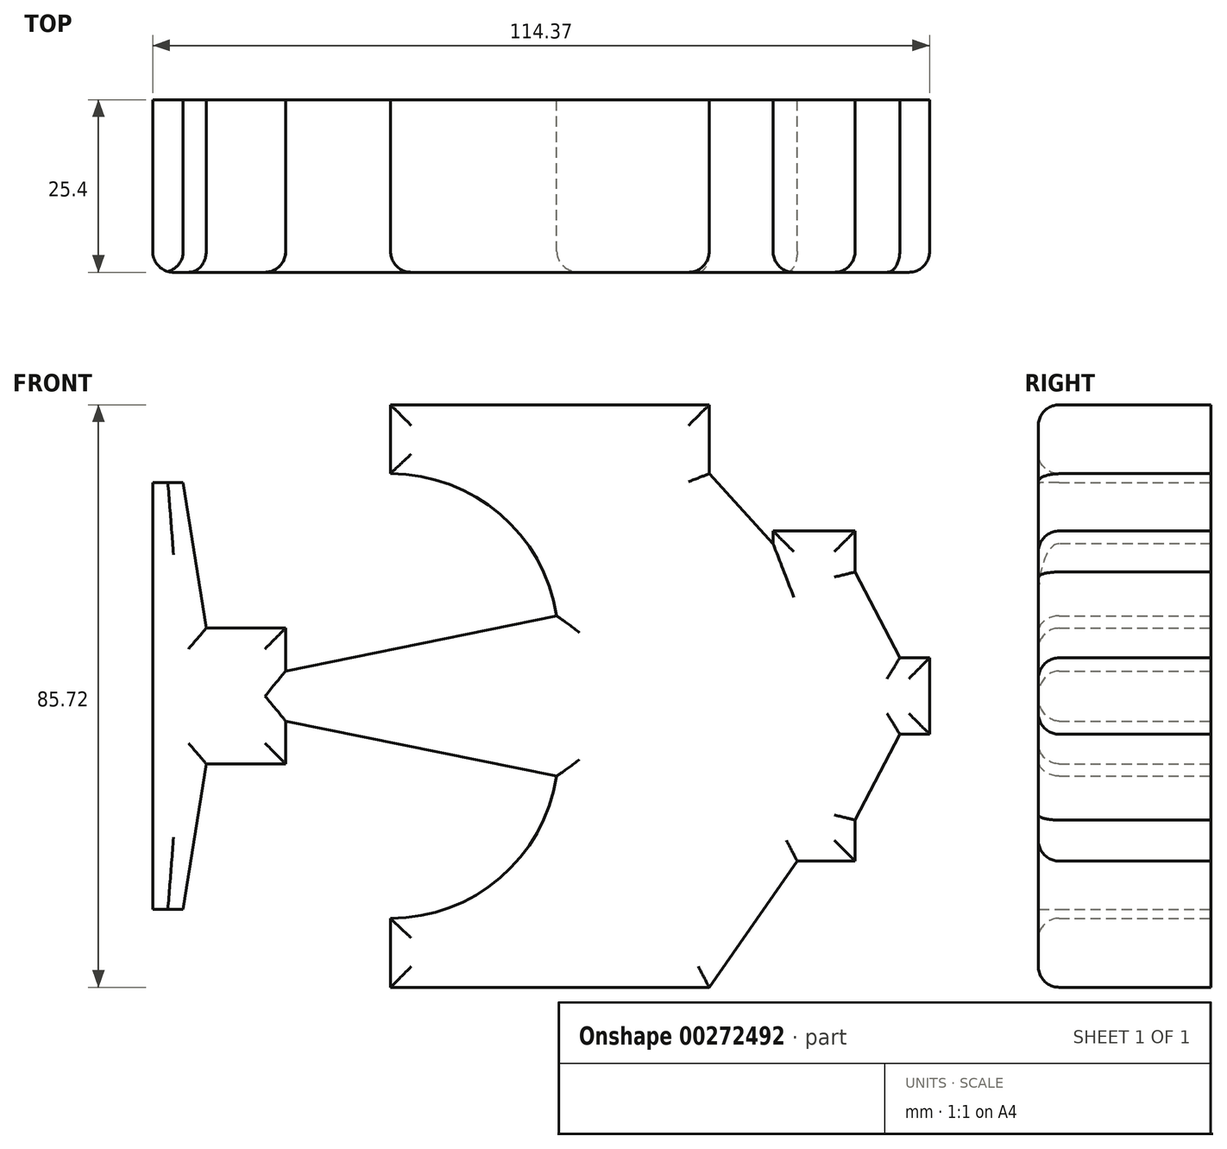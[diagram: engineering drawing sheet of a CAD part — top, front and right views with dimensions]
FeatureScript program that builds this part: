
annotation { "Feature Type Name" : "Feature", "Feature Type Description" : "" }
export const myFeature = defineFeature(function(context is Context, id is Id, definition is map)
    precondition{}
    {
        {
            var Q0;
            Q0=qCreatedBy(makeId("Front.planeOp"),FACE);
            var sketch = newSketch(context, id + "F0", { "sketchPlane" : qUnion([Q0])});
            skLineSegment(sketch, "E0.bottom", {"start": v(38.9, 3.7) * mm, "end": v(-38.9, 3.7) * mm});
            skLineSegment(sketch, "E0.top", {"start": v(38.9, -3.7) * mm, "end": v(-38.9, -3.7) * mm});
            skLineSegment(sketch, "E0.left", {"start": v(38.9, 3.7) * mm, "end": v(38.9, -3.7) * mm});
            skLineSegment(sketch, "E0.right", {"start": v(-38.9, 3.7) * mm, "end": v(-38.9, -3.7) * mm});
            skPoint(sketch, "E0.middle", {"position": v(0, 0) * mm});
            skLineSegment(sketch, "E1.bottom", {"start": v(32.86, -24.29) * mm, "end": v(44.93, -24.29) * mm});
            skLineSegment(sketch, "E1.top", {"start": v(32.86, -18.25) * mm, "end": v(44.93, -18.25) * mm});
            skLineSegment(sketch, "E1.left", {"start": v(32.86, -24.29) * mm, "end": v(32.86, -18.25) * mm});
            skLineSegment(sketch, "E1.right", {"start": v(44.93, -24.29) * mm, "end": v(44.93, -18.25) * mm});
            skPoint(sketch, "E1.middle", {"position": v(38.9, -21.27) * mm});
            skLineSegment(sketch, "E2.MirrorCS", {"start": v(32.86, 18.25) * mm, "end": v(44.93, 18.25) * mm});
            skPoint(sketch, "E3.MirrorP", {"position": v(38.9, 21.27) * mm});
            skLineSegment(sketch, "E4.MirrorCS", {"start": v(44.93, 24.29) * mm, "end": v(44.93, 18.25) * mm});
            skLineSegment(sketch, "E5.MirrorCS", {"start": v(32.86, 24.29) * mm, "end": v(32.86, 18.25) * mm});
            skLineSegment(sketch, "E6.MirrorCS", {"start": v(32.86, 24.29) * mm, "end": v(44.93, 24.29) * mm});
            skLineSegment(sketch, "E7", {"start": v(44.93, -18.25) * mm, "end": v(38.9, -3.7) * mm});
            skLineSegment(sketch, "E8", {"start": v(44.93, 18.25) * mm, "end": v(38.9, 3.7) * mm});
            skLineSegment(sketch, "E9", {"start": v(32.86, -18.25) * mm, "end": v(-38.9, -3.7) * mm});
            skLineSegment(sketch, "E10", {"start": v(32.86, 18.25) * mm, "end": v(-38.9, 3.7) * mm});
            skLineSegment(sketch, "E11.bottom", {"start": v(51.51, 5.61) * mm, "end": v(55.9, 5.61) * mm});
            skLineSegment(sketch, "E11.top", {"start": v(51.51, -5.61) * mm, "end": v(55.9, -5.61) * mm});
            skLineSegment(sketch, "E11.left", {"start": v(51.51, 5.61) * mm, "end": v(51.51, -5.61) * mm});
            skLineSegment(sketch, "E11.right", {"start": v(55.9, 5.61) * mm, "end": v(55.9, -5.61) * mm});
            skPoint(sketch, "E11.middle", {"position": v(53.7, 0) * mm});
            skLineSegment(sketch, "E12", {"start": v(51.51, 5.61) * mm, "end": v(44.93, 18.25) * mm});
            skLineSegment(sketch, "E13", {"start": v(51.51, -5.61) * mm, "end": v(44.93, -18.25) * mm});
            skLineSegment(sketch, "E14.bottom", {"start": v(-38.9, 9.99) * mm, "end": v(-38.9, 9.99) * mm});
            skLineSegment(sketch, "E14.top", {"start": v(-38.9, -9.99) * mm, "end": v(-38.9, -9.99) * mm});
            skLineSegment(sketch, "E14.left", {"start": v(-38.9, 9.99) * mm, "end": v(-38.9, -9.99) * mm});
            skLineSegment(sketch, "E14.right", {"start": v(-38.9, 9.99) * mm, "end": v(-38.9, -9.99) * mm});
            skPoint(sketch, "E14.middle", {"position": v(-38.9, 0) * mm});
            skLineSegment(sketch, "E15.bottom", {"start": v(-47.82, 9.99) * mm, "end": v(-50.58, 9.99) * mm});
            skLineSegment(sketch, "E15.top", {"start": v(-47.82, -9.99) * mm, "end": v(-50.58, -9.99) * mm});
            skLineSegment(sketch, "E15.left", {"start": v(-47.82, 9.99) * mm, "end": v(-47.82, -9.99) * mm});
            skLineSegment(sketch, "E15.right", {"start": v(-50.58, 9.99) * mm, "end": v(-50.58, -9.99) * mm});
            skPoint(sketch, "E15.middle", {"position": v(-49.2, 0) * mm});
            skLineSegment(sketch, "E16.bottom", {"start": v(-58.47, 31.4) * mm, "end": v(-53.98, 31.4) * mm});
            skLineSegment(sketch, "E16.top", {"start": v(-58.47, -31.4) * mm, "end": v(-53.98, -31.4) * mm});
            skLineSegment(sketch, "E16.left", {"start": v(-58.47, 31.4) * mm, "end": v(-58.47, -31.4) * mm});
            skLineSegment(sketch, "E16.right", {"start": v(-53.98, 31.4) * mm, "end": v(-53.98, -31.4) * mm});
            skPoint(sketch, "E16.middle", {"position": v(-56.22, 0) * mm});
            skLineSegment(sketch, "E17", {"start": v(-50.58, 9.99) * mm, "end": v(-53.98, 31.4) * mm});
            skLineSegment(sketch, "E18", {"start": v(-50.58, -9.99) * mm, "end": v(-53.98, -31.4) * mm});
            skLineSegment(sketch, "E19", {"start": v(-38.9, 9.99) * mm, "end": v(-50.58, 9.99) * mm});
            skLineSegment(sketch, "E20", {"start": v(-38.9, -9.99) * mm, "end": v(-47.82, -9.99) * mm});
            skSolve(sketch);
        }
        {
            var Q0;
            Q0 = qSketchRegion(id + "F0", true);
            extrude(context, id + "F1", {"entities" : qUnion([Q0]), "depth" : 25.4 * mm});
        }
        {
            var Q0;
            Q0=makeQuery(id+"F1.opExtrude","CAP_FACE",FACE,{"disambiguationData":[OSD([sQuery(id+"F0.wireOp",EDGE,"E1.bottom"),sQuery(id+"F0.wireOp",EDGE,"E1.left"),sQuery(id+"F0.wireOp",EDGE,"E1.right"),sQuery(id+"F0.wireOp",EDGE,"E4.MirrorCS"),sQuery(id+"F0.wireOp",EDGE,"E5.MirrorCS"),sQuery(id+"F0.wireOp",EDGE,"E6.MirrorCS"),sQuery(id+"F0.wireOp",EDGE,"E9"),sQuery(id+"F0.wireOp",EDGE,"E10"),sQuery(id+"F0.wireOp",EDGE,"E11.bottom"),sQuery(id+"F0.wireOp",EDGE,"E11.top"),sQuery(id+"F0.wireOp",EDGE,"E11.right"),sQuery(id+"F0.wireOp",EDGE,"E12"),sQuery(id+"F0.wireOp",EDGE,"E13"),sQuery(id+"F0.wireOp",EDGE,"E14.right"),sQuery(id+"F0.wireOp",EDGE,"E15.bottom"),sQuery(id+"F0.wireOp",EDGE,"E15.top"),sQuery(id+"F0.wireOp",EDGE,"E15.left"),sQuery(id+"F0.wireOp",EDGE,"E15.right"),sQuery(id+"F0.wireOp",EDGE,"goO5Bia0-x4cH-6lpz-OVmU-LoH8AdzGMyGm"),sQuery(id+"F0.wireOp",EDGE,"4VjyYicK-sjan-bqBq-XfXp-LJwPcruYnJMG"),sQuery(id+"F0.wireOp",EDGE,"eEolKJ5h-S5Iy-8XED-Ycb1-uaVqnnNI2b9E"),sQuery(id+"F0.wireOp",EDGE,"oFdVb1Zb-m78f-jIjX-JeHE-OYrAXJyPXflU")])],"isStart":false});
            fillet(context, id + "F2", {"entities" : qUnion([Q0]), "radius" : 2.45 * mm, "tangentPropagation" : true, "allowEdgeOverflow" : false});
        }
        {
            var Q0;
            Q0=qCreatedBy(makeId("Front.planeOp"),FACE);
            var sketch = newSketch(context, id + "F3", { "sketchPlane" : qUnion([Q0])});
            skLineSegment(sketch, "E21.bottom", {"start": v(-23.45, -42.86) * mm, "end": v(23.45, -42.86) * mm});
            skLineSegment(sketch, "E21.top", {"start": v(-23.45, -32.71) * mm, "end": v(23.45, -32.71) * mm});
            skLineSegment(sketch, "E21.left", {"start": v(-23.45, -42.86) * mm, "end": v(-23.45, -32.71) * mm});
            skLineSegment(sketch, "E21.right", {"start": v(23.45, -42.86) * mm, "end": v(23.45, -32.71) * mm});
            skPoint(sketch, "E21.middle", {"position": v(0, -37.79) * mm});
            skPoint(sketch, "E22.MirrorP", {"position": v(0, 37.79) * mm});
            skLineSegment(sketch, "E23.MirrorCS", {"start": v(23.45, 42.86) * mm, "end": v(23.45, 32.71) * mm});
            skLineSegment(sketch, "E24.MirrorCS", {"start": v(-23.45, 42.86) * mm, "end": v(-23.45, 32.71) * mm});
            skLineSegment(sketch, "E25.MirrorCS", {"start": v(-23.45, 32.71) * mm, "end": v(23.45, 32.71) * mm});
            skLineSegment(sketch, "E26.MirrorCS", {"start": v(-23.45, 42.86) * mm, "end": v(23.45, 42.86) * mm});
            skLineSegment(sketch, "E27", {"start": v(23.45, 32.71) * mm, "end": v(53.36, 0) * mm});
            skLineSegment(sketch, "E28", {"start": v(53.36, 0) * mm, "end": v(23.45, -42.86) * mm});
            skArc(sketch, "E29", {"start": v(0, 0) * mm, "mid": v(-3.33, 22.38) * mm, "end": v(-23.45, 32.71) * mm});
            skArc(sketch, "E30", {"start": v(-23.45, -32.71) * mm, "mid": v(-3.33, -22.38) * mm, "end": v(0, 0) * mm});
            skSolve(sketch);
        }
        {
            var Q0;
            Q0 = qSketchRegion(id + "F3", true);
            extrude(context, id + "F4", {"entities" : qUnion([Q0]), "operationType" : NewBodyOperationType.ADD, "depth" : 25.4 * mm});
        }
        {
            var Q0;
            Q0 = qSketchRegion(id + "F0", true);
            extrude(context, id + "F5", {"entities" : qUnion([Q0]), "operationType" : NewBodyOperationType.ADD, "depth" : 25.4 * mm});
        }
        {
            var Q0;
            Q0 = qSketchRegion(id + "F0", true);
            extrude(context, id + "F6", {"entities" : qUnion([Q0]), "operationType" : NewBodyOperationType.ADD, "depth" : 25.4 * mm});
        }
        {
            var Q0;
            {var subQ0=sQuery(id+"F0.wireOp",EDGE,"E20");var subQ1=sQuery(id+"F0.wireOp",EDGE,"E19");var subQ2=sQuery(id+"F0.wireOp",EDGE,"E18");var subQ3=sQuery(id+"F0.wireOp",EDGE,"E17");var subQ4=sQuery(id+"F0.wireOp",EDGE,"E16.left");var subQ5=sQuery(id+"F0.wireOp",EDGE,"E16.top");var subQ6=sQuery(id+"F0.wireOp",EDGE,"E16.bottom");var subQ7=sQuery(id+"F0.wireOp",EDGE,"E15.top");var subQ8=sQuery(id+"F0.wireOp",EDGE,"E14.right");var subQ9=sQuery(id+"F0.wireOp",EDGE,"E13");var subQ10=sQuery(id+"F0.wireOp",EDGE,"E12");var subQ11=sQuery(id+"F0.wireOp",EDGE,"E11.right");var subQ12=sQuery(id+"F0.wireOp",EDGE,"E11.top");var subQ13=sQuery(id+"F0.wireOp",EDGE,"E11.bottom");var subQ14=sQuery(id+"F0.wireOp",EDGE,"E10");var subQ15=sQuery(id+"F0.wireOp",EDGE,"E9");var subQ16=sQuery(id+"F0.wireOp",EDGE,"E6.MirrorCS");var subQ17=sQuery(id+"F0.wireOp",EDGE,"E5.MirrorCS");var subQ18=sQuery(id+"F0.wireOp",EDGE,"E4.MirrorCS");var subQ19=sQuery(id+"F0.wireOp",EDGE,"E1.right");var subQ20=sQuery(id+"F0.wireOp",EDGE,"E1.left");var subQ21=sQuery(id+"F0.wireOp",EDGE,"E1.bottom");Q0=makeQuery(id+"F5.boolean.opBoolean","MERGE",FACE,{"derivedFrom":[makeQuery(id+"F4.boolean.opBoolean","MERGE",FACE,{"derivedFrom":[makeQuery(id+"F1.opExtrude","CAP_FACE",FACE,{"disambiguationData":[OSD([subQ21,subQ20,subQ19,subQ18,subQ17,subQ16,subQ15,subQ14,subQ13,subQ12,subQ11,subQ10,subQ9,subQ8,subQ7,subQ6,subQ5,subQ4,subQ3,subQ2,subQ1,subQ0])],"isStart":false}),makeQuery(id+"F4.opExtrude","CAP_FACE",FACE,{"disambiguationData":[OSD([sQuery(id+"F3.wireOp",EDGE,"E21.bottom"),sQuery(id+"F3.wireOp",EDGE,"E21.left"),sQuery(id+"F3.wireOp",EDGE,"E23.MirrorCS"),sQuery(id+"F3.wireOp",EDGE,"E24.MirrorCS"),sQuery(id+"F3.wireOp",EDGE,"E26.MirrorCS"),sQuery(id+"F3.wireOp",EDGE,"E27"),sQuery(id+"F3.wireOp",EDGE,"E28"),sQuery(id+"F3.wireOp",EDGE,"E29"),sQuery(id+"F3.wireOp",EDGE,"E30")])],"isStart":false})]}),makeQuery(id+"F5.opExtrude","CAP_FACE",FACE,{"disambiguationData":[OSD([subQ21,subQ20,subQ19,subQ18,subQ17,subQ16,subQ15,subQ14,subQ13,subQ12,subQ11,subQ10,subQ9,subQ8,subQ7,subQ6,subQ5,subQ4,subQ3,subQ2,subQ1,subQ0])],"isStart":false})]});}
            fillet(context, id + "F7", {"entities" : qUnion([Q0]), "radius" : 3.07 * mm, "tangentPropagation" : true, "allowEdgeOverflow" : false});
        }
    });
